# Revit family: Lighting-Flush_Mount-Tech_Lighting-Crest_12
name_source: partatom
category: Lighting Fixtures
revit_build: Autodesk Revit 2017 (Build: 20160225_1515(x64)
units: mm (PartAtom-declared; Revit-internal decimal feet)

## family parameters
Cut with Voids When Loaded = No
Host = Face
Light Source = Yes
OmniClass Number = 23.80.70.11
OmniClass Title = Luminaries for Internal Lighting
Part Type = Normal
Room Calculation Point = No
Round Connector Dimension = Use Diameter
Shared = No

## types (4) — shared parameters
Apparent Load = 32 VA
Assembly Code = D5020200
CRI, CCT = 90 CRI, 3000K
Color Filter = 16777215
Controls = Consult Product Documentation
Default Elevation = 0' - 0"
Description = Crest 12 Ceiling Flush Mount
Dimming = Yes
Dimming Lamp Color Temperature Shift = <None>
Emit Shape Visible in Rendering = No
Emit from Circle Diameter = 0' - 11 9/16"
Environment = Suitable for Indoor Damp Locations
Frequency = 0 Hz
Height = 0' - 1 13/16"
Instruction Sheet Link = http://www.techlighting.com
Lamp = LED
Length = 1' - 0 5/16"
Lens = Glass - Tech Lighting - LED Lens
Load Classification = Lighting
Manufacturer = Tech Lighting
Manufacturer Fax Number = 847.410.4500
Model = 700FMCRST12xxx
Mounting = Flush Mount Ceiling
Number of Poles = 1
Output = 660 Lumens
Performance URL = Contact Tech Lighting for Performance Data
Phase = 1
Photometric Web File = 15111- CREST 12 FLUSH MOUNT.ies
Photometry Note = Please load ies file listed under Photometric Web File for accurate rendering.
Power Factor = 1
Product Documentation Link = http://www.techlighting.com
Product Name = Crest 12 Ceiling - 700FMCRST
Product Page URL = http://www.techlighting.com
Tilt Angle = 90.00°
Title 20 Compliant = Yes
Title 24 Compliant = Yes
URL = http://www.techlighting.com
Version = 2017 - v1.0a
Warranty URL = http://www.techlighting.com
Wattage Comments = (1) 32 Watts
Width = 1' - 0 5/16"

## per-type parameters (varying)
| type | Finish | Voltage | Voltage Comment |
| 700FMCRST12S-LED930 | Metal - Tech Lighting - Satin Nickel | 120 V | 120 Volts |
| 700FMCRST12S-LED930-277 | Metal - Tech Lighting - Satin Nickel | 277 V | 277 Volts |
| 700FMCRST12W-LED930 | Metal - Tech Lighting - Matte White | 120 V | 120 Volts |
| 700FMCRST12W-LED930-277 | Metal - Tech Lighting - Matte White | 277 V | 277 Volts |

## geometry (parser evidence)
native form markers: Sweep x3
no freeform markers — native parametric forms only
